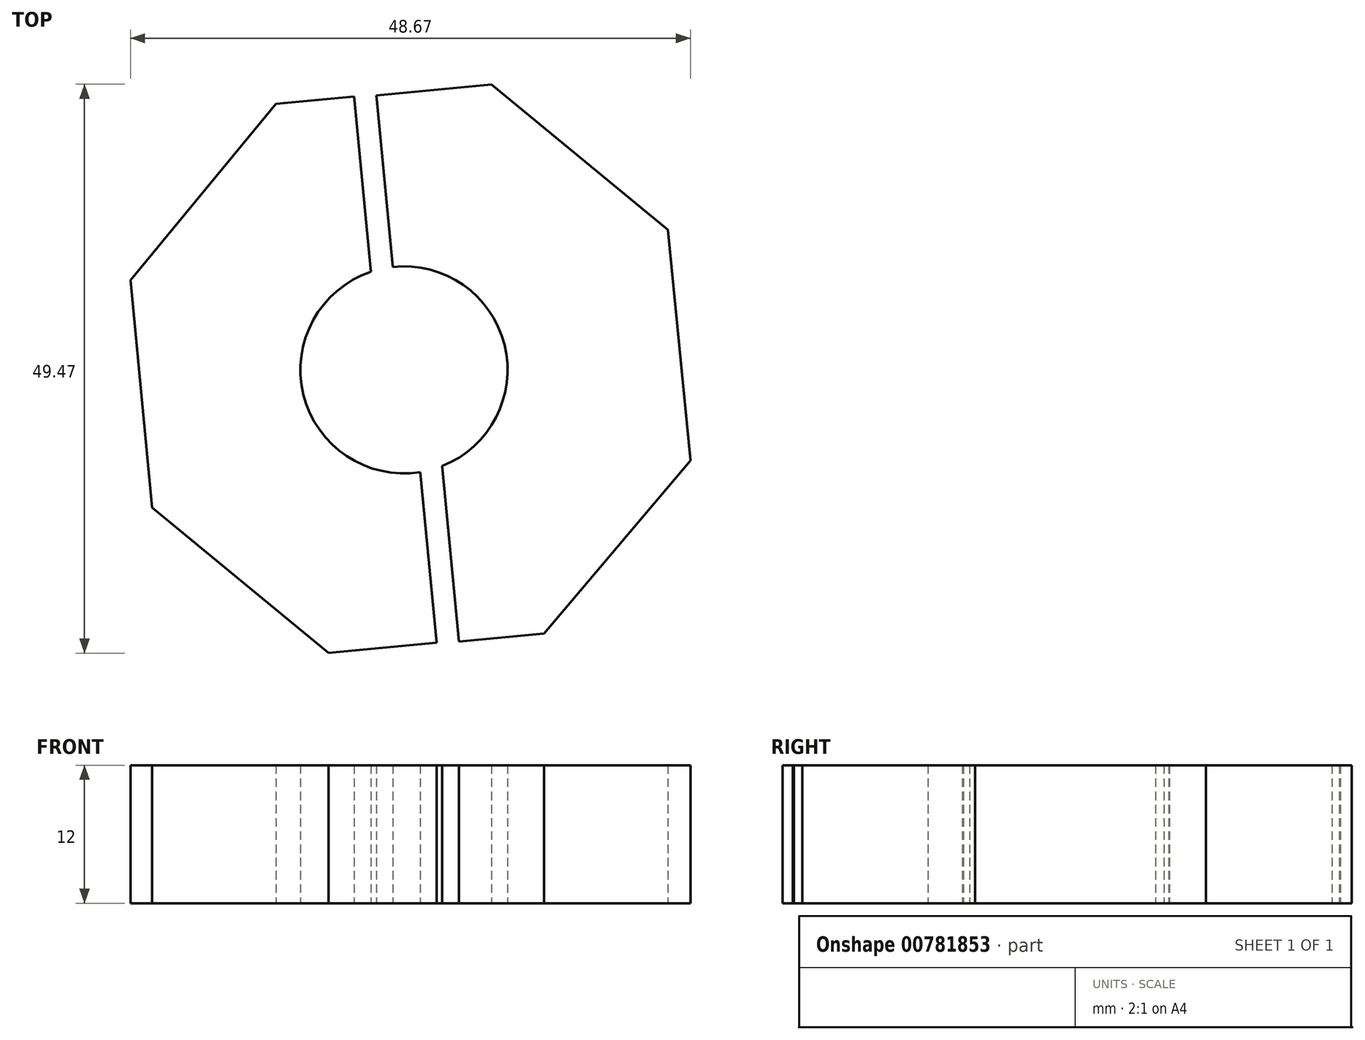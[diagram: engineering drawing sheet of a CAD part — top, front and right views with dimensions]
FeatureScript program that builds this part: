
annotation { "Feature Type Name" : "Feature", "Feature Type Description" : "" }
export const myFeature = defineFeature(function(context is Context, id is Id, definition is map)
    precondition{}
    {
        {
            var Q0;
            Q0=qCreatedBy(makeId("Top.planeOp"),FACE);
            var sketch = newSketch(context, id + "F0", { "sketchPlane" : qUnion([Q0])});
            skLineSegment(sketch, "E0.0", {"start": v(2.8, 27.25) * mm, "end": v(-7.22, 26.28) * mm});
            skLineSegment(sketch, "E0.1", {"start": v(18.12, 14.6) * mm, "end": v(2.8, 27.25) * mm});
            skLineSegment(sketch, "E0.7", {"start": v(-7.22, 26.28) * mm, "end": v(-6.05, 14.15) * mm});
            skLineSegment(sketch, "E0.9", {"start": v(-1.24, -8.48) * mm, "end": v(-0.02, -21.22) * mm});
            skLineSegment(sketch, "E0.10", {"start": v(-0.02, -21.22) * mm, "end": v(7.38, -20.5) * mm});
            skPoint(sketch, "E0.16", {"position": v(-0.63, -14.85) * mm});
            skLineSegment(sketch, "E1.3", {"start": v(-15.94, 25.53) * mm, "end": v(-28.58, 10.2) * mm});
            skLineSegment(sketch, "E1.4", {"start": v(-9.15, 26.19) * mm, "end": v(-15.94, 25.53) * mm});
            skLineSegment(sketch, "E1.5", {"start": v(-7.87, 12.77) * mm, "end": v(-9.15, 26.19) * mm});
            skLineSegment(sketch, "E1.6", {"start": v(-28.58, 10.2) * mm, "end": v(-26.68, -9.57) * mm});
            skLineSegment(sketch, "E1.7", {"start": v(-26.68, -9.57) * mm, "end": v(-11.35, -22.22) * mm});
            skLineSegment(sketch, "E1.8", {"start": v(-11.35, -22.22) * mm, "end": v(-1.97, -21.32) * mm});
            skLineSegment(sketch, "E1.9", {"start": v(-1.97, -21.32) * mm, "end": v(-3.16, -8.95) * mm});
            skLineSegment(sketch, "E2", {"start": v(-6.05, 14.15) * mm, "end": v(-5.76, 11.1) * mm});
            skLineSegment(sketch, "E3", {"start": v(-1.24, -8.48) * mm, "end": v(-1.51, -5.7) * mm});
            skLineSegment(sketch, "E4", {"start": v(-3.16, -8.95) * mm, "end": v(-3.42, -6.23) * mm});
            skLineSegment(sketch, "E5", {"start": v(-7.87, 12.77) * mm, "end": v(-7.67, 10.68) * mm});
            skLineSegment(sketch, "E6", {"start": v(7.38, -20.5) * mm, "end": v(20.1, -5.48) * mm});
            skLineSegment(sketch, "E7", {"start": v(20.1, -5.48) * mm, "end": v(18.12, 14.6) * mm});
            skCircle(sketch, "E8", {"center": v(-4.8, 2.41) * mm, "radius": 9 * mm});
            skSolve(sketch);
        }
        {
            var Q0;
            {var subQ3=sQuery(id+"F0.wireOp",EDGE,"E4");Q0=makeQuery(id+"F0.imprint","IMPRINT",FACE,{"disambiguationData":[TD([[makeQuery(id+"F0.imprint","IMPRINT",EDGE,{"derivedFrom":subQ3}),1.0]])]});}
            var Q1;
            {var subQ2=sQuery(id+"F0.wireOp",EDGE,"E2");Q1=makeQuery(id+"F0.imprint","IMPRINT",FACE,{"disambiguationData":[TD([[makeQuery(id+"F0.imprint","IMPRINT",EDGE,{"derivedFrom":subQ2}),1.0]])]});}
            extrude(context, id + "F1", {"entities" : qUnion([Q0, Q1]), "depth" : 12 * mm, "offsetDistance" : 25 * mm});
        }
    });
